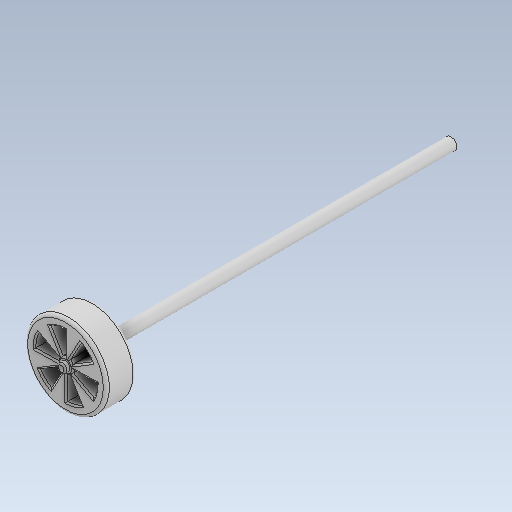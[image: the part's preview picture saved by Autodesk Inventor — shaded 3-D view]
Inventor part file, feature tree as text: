
AUTODESK INVENTOR PART (.ipt)
format: ipt  version: 2021 (Build 250183000, 183)  size: 290,816 bytes
history: native  units: mm
features: sketch x6, extrude x5, fillet x3, pattern_circular x1, hole x1
ambient origin geometry x8: Origin, YZ Plane, XZ Plane, XY Plane, X Axis, Y Axis, Z Axis, Center Point
bodies: Solid1 (feature_tree)
feature tree (16):
  extrude  "Extrusion1"  Depth=20.0mm TaperAngle=0.0deg
  fillet  "Fillet1"  Radius=2.0mm
  extrude  "Extrusion2"  Depth=10.0mm
  fillet  "Fillet2"  [1 undecoded]
  pattern_circular  "Circular Pattern1"  Count=6 Angle=360.0deg
  extrude  "Extrusion3"  Depth=3.0mm TaperAngle=0.0deg
  fillet  "Fillet3"  Radius=1.0mm
  hole  "Hole1"  [1 undecoded]
  extrude  "Extrusion4"  Depth=260.0mm TaperAngle=0.0deg
  extrude  "Extrusion5"  [1 undecoded]
  sketch  "Sketch1"  dims[d0=55.0mm d1=20.0mm d2=0.0mm d3=2.0mm]
  sketch  "Sketch2"  dims[d4=42.0mm d5=10.0mm d6=30.0deg]
  sketch  "Sketch3"  dims[d7=0.0mm d8=0.0mm]
  sketch  "Sketch4"  dims[d9=1.0mm d10=60.0mm d11=360.0deg]
  sketch  "Sketch5"  dims[d13=6.0mm d14=3.0mm d15=0.0mm d16=1.0mm]
  sketch  "Sketch6"  dims[d17=4.0mm d18=6.0mm d19=4.0mm d20=2.0mm d21=90.0deg d22=8.0mm d23=20.594885mm d24=260.0mm d25=0.0mm d26=260.0mm d27=0.0mm]
note: 3 required parameter values undecoded (feature->parameter linkage not recoverable at this tier; creation-order binding heuristic only, values carry confidence <= 0.55)
